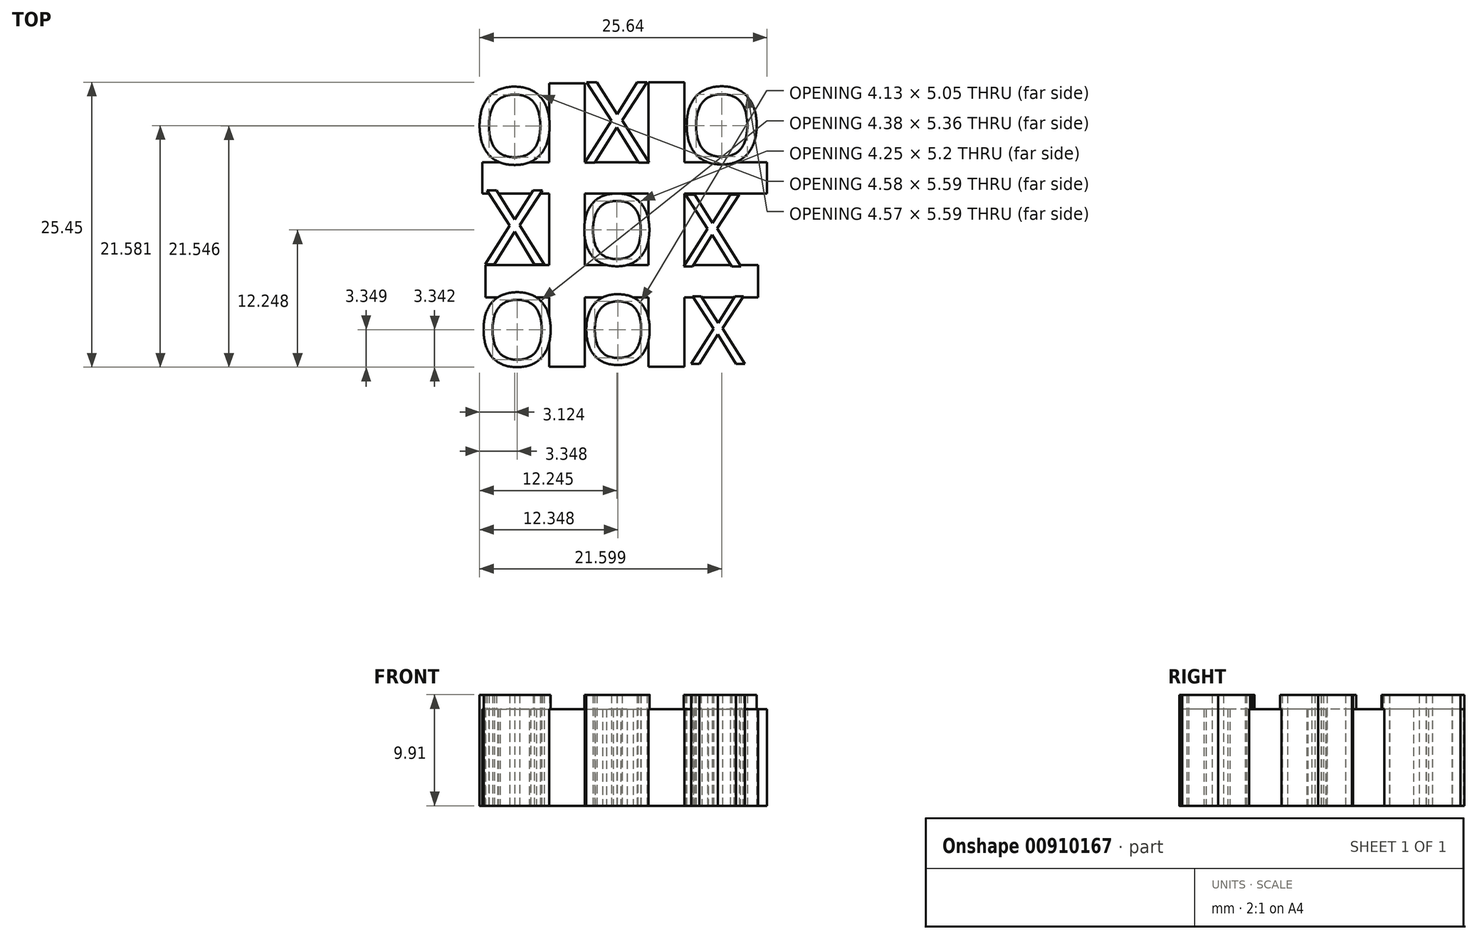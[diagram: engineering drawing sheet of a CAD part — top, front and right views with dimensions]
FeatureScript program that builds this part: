
annotation { "Feature Type Name" : "Feature", "Feature Type Description" : "" }
export const myFeature = defineFeature(function(context is Context, id is Id, definition is map)
    precondition{}
    {
        {
            var Q0;
            Q0=qCreatedBy(makeId("Top.planeOp"),FACE);
            var sketch = newSketch(context, id + "F0", { "sketchPlane" : qUnion([Q0])});
            skLineSegment(sketch, "E0.bottom", {"start": v(-7.99, 11.1) * mm, "end": v(-4.8, 11.1) * mm});
            skLineSegment(sketch, "E0.top", {"start": v(-7.99, -14.2) * mm, "end": v(-4.8, -14.2) * mm});
            skLineSegment(sketch, "E0.left", {"start": v(-7.99, 11.1) * mm, "end": v(-7.99, -14.2) * mm});
            skLineSegment(sketch, "E0.right", {"start": v(-4.8, 11.1) * mm, "end": v(-4.8, -14.2) * mm});
            skLineSegment(sketch, "E1.bottom", {"start": v(0.88, 11.2) * mm, "end": v(4.06, 11.2) * mm});
            skLineSegment(sketch, "E1.top", {"start": v(0.88, -14.2) * mm, "end": v(4.06, -14.2) * mm});
            skLineSegment(sketch, "E1.left", {"start": v(0.88, 11.2) * mm, "end": v(0.88, -14.2) * mm});
            skLineSegment(sketch, "E1.right", {"start": v(4.06, 11.2) * mm, "end": v(4.06, -14.2) * mm});
            skLineSegment(sketch, "E2.bottom", {"start": v(-13.96, 4.03) * mm, "end": v(11.44, 4.03) * mm});
            skLineSegment(sketch, "E2.top", {"start": v(-13.96, 1.24) * mm, "end": v(11.44, 1.24) * mm});
            skLineSegment(sketch, "E2.left", {"start": v(-13.96, 4.03) * mm, "end": v(-13.96, 1.24) * mm});
            skLineSegment(sketch, "E2.right", {"start": v(11.44, 4.03) * mm, "end": v(11.44, 1.24) * mm});
            skLineSegment(sketch, "E3.bottom", {"start": v(-13.67, -5.13) * mm, "end": v(10.64, -5.13) * mm});
            skLineSegment(sketch, "E3.top", {"start": v(-13.67, -8.02) * mm, "end": v(10.64, -8.02) * mm});
            skLineSegment(sketch, "E3.left", {"start": v(-13.67, -5.13) * mm, "end": v(-13.67, -8.02) * mm});
            skLineSegment(sketch, "E3.right", {"start": v(10.64, -5.13) * mm, "end": v(10.64, -8.02) * mm});
            skSolve(sketch);
        }
        {
            var Q0;
            Q0 = qSketchRegion(id + "F0", true);
            extrude(context, id + "F1", {"entities" : qUnion([Q0]), "depth" : 8.64 * mm, "offsetDistance" : 25.4 * mm});
        }
        {
            var Q0;
            Q0=qCreatedBy(makeId("Top.planeOp"),FACE);
            var sketch = newSketch(context, id + "F2", { "sketchPlane" : qUnion([Q0])});
            skText(sketch, "E4", { "text": "X", "fontName": "OpenSans-Regular.ttf"});
            skText(sketch, "E5", { "text": "O", "fontName": "OpenSans-Regular.ttf"});
            skText(sketch, "E6", { "text": "X", "fontName": "OpenSans-Regular.ttf"});
            skText(sketch, "E7", { "text": "O", "fontName": "OpenSans-Regular.ttf"});
            skText(sketch, "E8", { "text": "X", "fontName": "OpenSans-Regular.ttf"});
            skText(sketch, "E9", { "text": "O", "fontName": "OpenSans-Regular.ttf"});
            skText(sketch, "E10", { "text": "O", "fontName": "OpenSans-Regular.ttf"});
            skText(sketch, "E11", { "text": "X", "fontName": "OpenSans-Regular.ttf"});
            skText(sketch, "E12", { "text": "O", "fontName": "OpenSans-Regular.ttf"});
            const initialGuessF2  = {"E4": [-0.00485, 0.004, 1, 0, 0.00725], "E5": [-0.01478, 0.0039, 1, 0, 0.00685], "E6": [-0.01374, -0.00506, 1, 0, 0.00666], "E7": [-0.0054, -0.00516, 1, 0, 0.00637], "E8": [0.00398, -0.00525, 1, 0, 0.00647], "E9": [-0.0144, -0.01416, 1, 0, 0.00656], "E10": [-0.0052, -0.01397, 1, 0, 0.00619], "E11": [0.00463, -0.01397, 1, 0, 0.0061], "E12": [0.0037, 0.00394, 1, 0, 0.00684]};
            skSetInitialGuess(sketch, initialGuessF2);
            skSolve(sketch);
        }
        {
            var Q0;
            Q0 = qSketchRegion(id + "F2", true);
            extrude(context, id + "F3", {"entities" : qUnion([Q0]), "operationType" : NewBodyOperationType.ADD, "depth" : 9.9 * mm, "offsetDistance" : 25.4 * mm});
        }
    });
